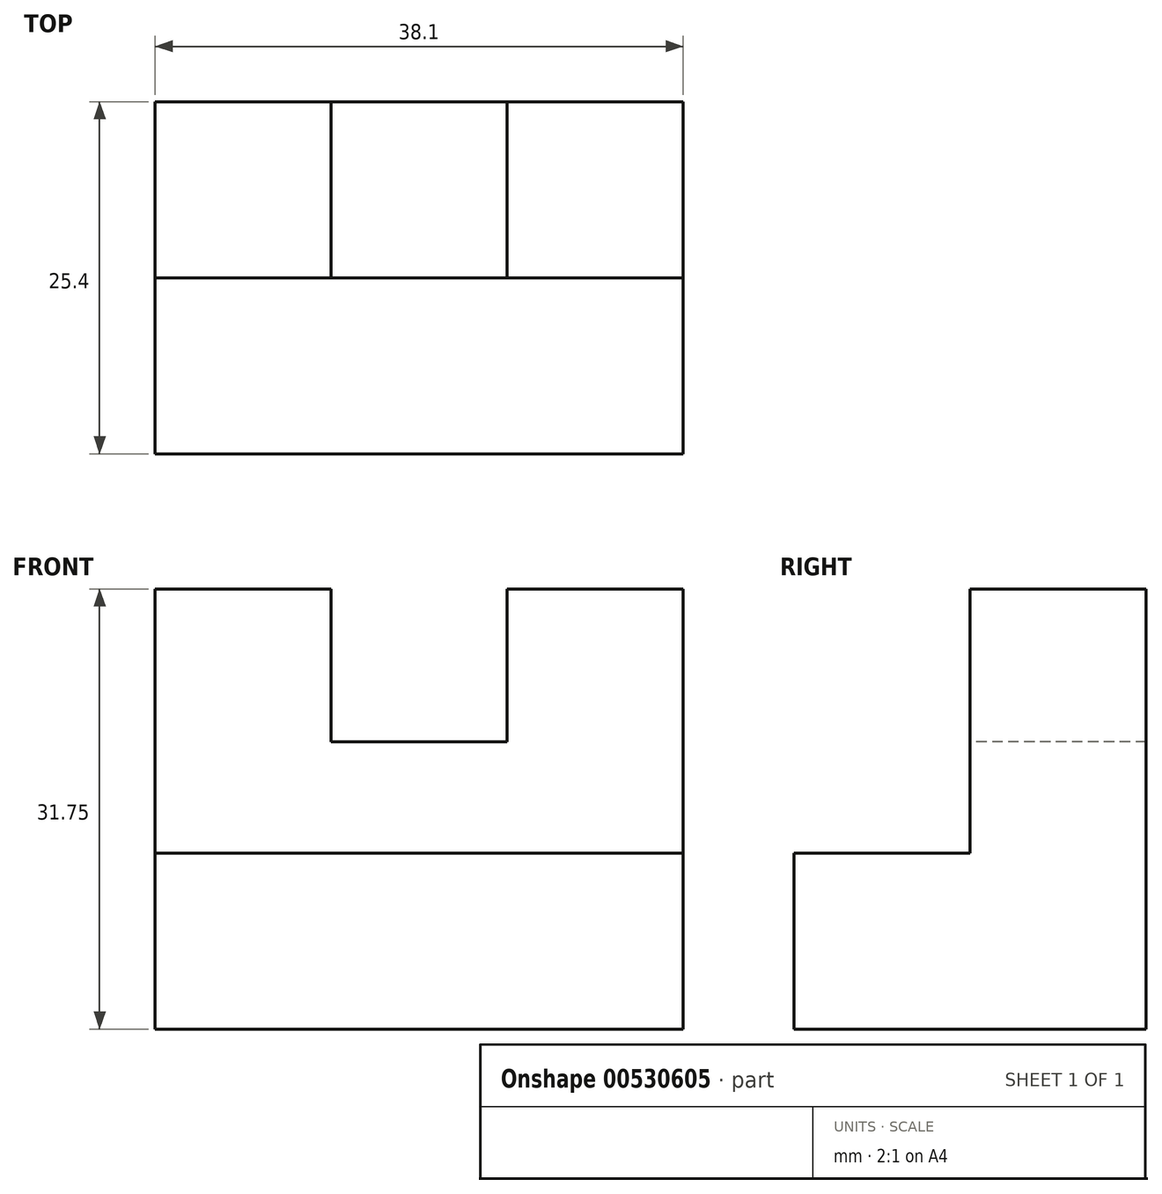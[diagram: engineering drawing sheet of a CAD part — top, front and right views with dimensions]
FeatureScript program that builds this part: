
annotation { "Feature Type Name" : "Feature", "Feature Type Description" : "" }
export const myFeature = defineFeature(function(context is Context, id is Id, definition is map)
    precondition{}
    {
        {
            var Q0;
            Q0=qCreatedBy(makeId("Right.planeOp"),FACE);
            var sketch = newSketch(context, id + "F0", { "sketchPlane" : qUnion([Q0])});
            skLineSegment(sketch, "E0", {"start": v(0, 31.75) * mm, "end": v(0, 0) * mm});
            skLineSegment(sketch, "E1", {"start": v(0, 0) * mm, "end": v(-25.4, 0) * mm});
            skLineSegment(sketch, "E2", {"start": v(-25.4, 0) * mm, "end": v(-25.4, 12.7) * mm});
            skLineSegment(sketch, "E3", {"start": v(-25.4, 12.7) * mm, "end": v(-12.7, 12.7) * mm});
            skLineSegment(sketch, "E4", {"start": v(-12.7, 12.7) * mm, "end": v(-12.7, 31.75) * mm});
            skLineSegment(sketch, "E5", {"start": v(-12.7, 31.75) * mm, "end": v(0, 31.75) * mm});
            skSolve(sketch);
        }
        {
            var Q0;
            Q0 = qSketchRegion(id + "F0", true);
            extrude(context, id + "F1", {"entities" : qUnion([Q0]), "depth" : 38.1 * mm, "offsetDistance" : 25.4 * mm});
        }
        {
            var Q0;
            Q0=makeQuery(id+"F1.opExtrude","SWEPT_FACE",FACE,{"disambiguationData":[OSD([sQuery(id+"F0.wireOp",EDGE,"E4")])]});
            var sketch = newSketch(context, id + "F2", { "sketchPlane" : qUnion([Q0])});
            skLineSegment(sketch, "E6", {"start": v(12.7, 31.75) * mm, "end": v(12.7, 20.7) * mm});
            skLineSegment(sketch, "E7", {"start": v(12.7, 20.7) * mm, "end": v(25.4, 20.7) * mm});
            skLineSegment(sketch, "E8", {"start": v(25.4, 20.7) * mm, "end": v(25.4, 31.75) * mm});
            skSolve(sketch);
        }
        {
            var Q0;
            Q0 = qSketchRegion(id + "F2", true);
            var Q1;
            {var subQ0=sQuery(id+"F2.wireOp",EDGE,"E6");Q1=makeQuery(id+"F2.imprint","IMPRINT",FACE,{"disambiguationData":[TD([[makeQuery(id+"F2.imprint","IMPRINT",EDGE,{"derivedFrom":subQ0}),1.0]])]});}
            extrude(context, id + "F3", {"entities" : qUnion([Q0, Q1]), "operationType" : NewBodyOperationType.REMOVE, "endBound" : BoundingType.THROUGH_ALL, "oppositeDirection" : true, "depth" : 25.4 * mm, "offsetDistance" : 25.4 * mm});
        }
    });
